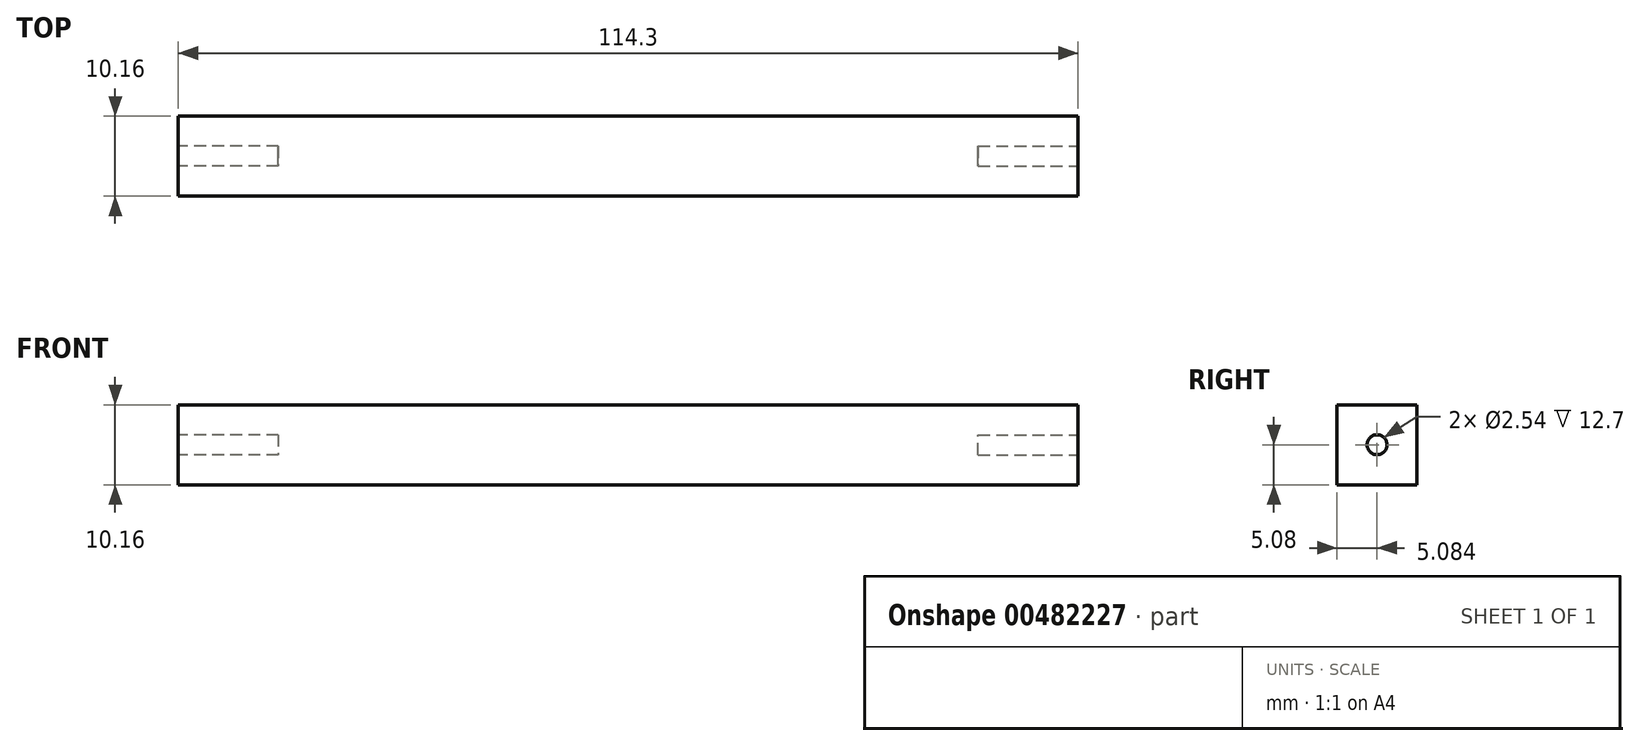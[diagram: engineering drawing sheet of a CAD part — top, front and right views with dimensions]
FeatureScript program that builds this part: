
annotation { "Feature Type Name" : "Feature", "Feature Type Description" : "" }
export const myFeature = defineFeature(function(context is Context, id is Id, definition is map)
    precondition{}
    {
        {
            var Q0;
            Q0=qCreatedBy(makeId("Top.planeOp"),FACE);
            var sketch = newSketch(context, id + "F0", { "sketchPlane" : qUnion([Q0])});
            skLineSegment(sketch, "E0.bottom", {"start": v(-61.17, 14.02) * mm, "end": v(53.13, 14.02) * mm});
            skLineSegment(sketch, "E0.top", {"start": v(-61.17, 3.86) * mm, "end": v(53.13, 3.86) * mm});
            skLineSegment(sketch, "E0.left", {"start": v(-61.17, 14.02) * mm, "end": v(-61.17, 3.86) * mm});
            skLineSegment(sketch, "E0.right", {"start": v(53.13, 14.02) * mm, "end": v(53.13, 3.86) * mm});
            skSolve(sketch);
        }
        {
            var Q0;
            Q0=makeQuery(id+"F0.imprint","IMPRINT",FACE,{"disambiguationData":[TD([[makeQuery(id+"F0.imprint","IMPRINT",EDGE,{"derivedFrom":sQuery(id+"F0.wireOp",EDGE,"E0.bottom")}),-1.0]])]});
            extrude(context, id + "F1", {"entities" : qUnion([Q0]), "depth" : 10.16 * mm, "offsetDistance" : 25.4 * mm});
        }
        {
            var Q0;
            Q0=makeQuery(id+"F1.opExtrude","SWEPT_FACE",FACE,{"disambiguationData":[OSD([sQuery(id+"F0.wireOp",EDGE,"E0.left")])]});
            var sketch = newSketch(context, id + "F2", { "sketchPlane" : qUnion([Q0])});
            skCircle(sketch, "E1", {"center": v(-8.94, 5.08) * mm, "radius": 1.27 * mm});
            skSolve(sketch);
        }
        {
            var Q0;
            Q0=makeQuery(id+"F1.opExtrude","SWEPT_FACE",FACE,{"disambiguationData":[OSD([sQuery(id+"F0.wireOp",EDGE,"E0.right")])]});
            var sketch = newSketch(context, id + "F3", { "sketchPlane" : qUnion([Q0])});
            skCircle(sketch, "E2", {"center": v(8.94, 5.08) * mm, "radius": 1.27 * mm});
            skSolve(sketch);
        }
        {
            var Q0;
            Q0=makeQuery(id+"F3.imprint","IMPRINT",FACE,{"disambiguationData":[TD([[makeQuery(id+"F3.imprint","IMPRINT",EDGE,{"derivedFrom":sQuery(id+"F3.wireOp",EDGE,"E2")}),1.0]])]});
            extrude(context, id + "F4", {"entities" : qUnion([Q0]), "operationType" : NewBodyOperationType.REMOVE, "oppositeDirection" : true, "depth" : 12.7 * mm, "offsetDistance" : 25.4 * mm});
        }
        {
            var Q0;
            Q0=makeQuery(id+"F2.imprint","IMPRINT",FACE,{"disambiguationData":[TD([[makeQuery(id+"F2.imprint","IMPRINT",EDGE,{"derivedFrom":sQuery(id+"F2.wireOp",EDGE,"E1")}),1.0]])]});
            extrude(context, id + "F5", {"entities" : qUnion([Q0]), "operationType" : NewBodyOperationType.REMOVE, "oppositeDirection" : true, "depth" : 12.7 * mm, "offsetDistance" : 25.4 * mm});
        }
    });
